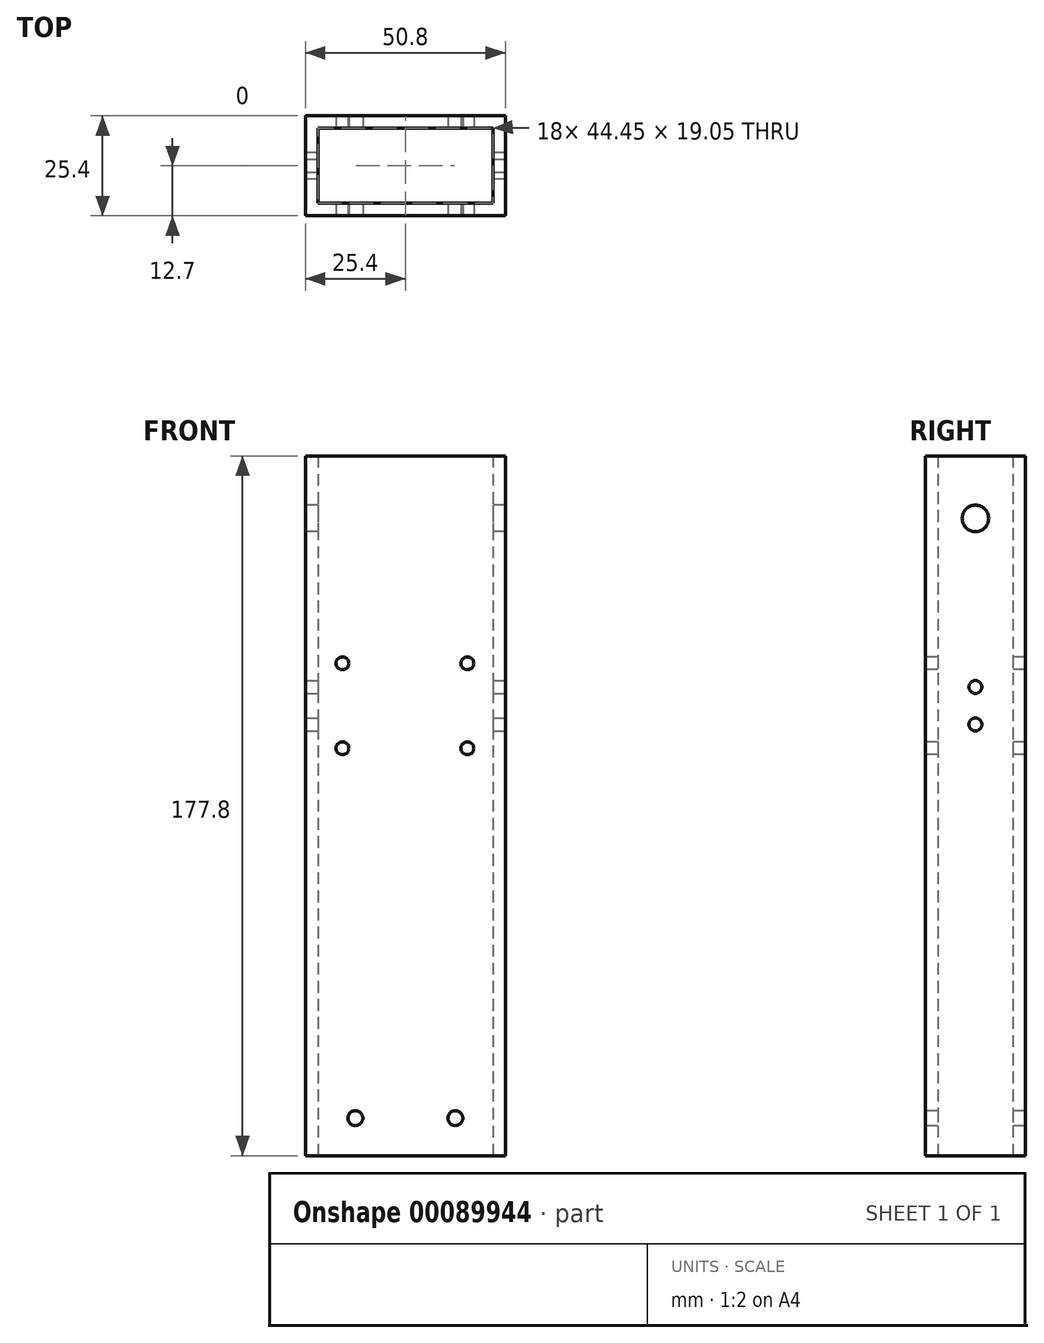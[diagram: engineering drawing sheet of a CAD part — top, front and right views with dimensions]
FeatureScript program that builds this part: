
annotation { "Feature Type Name" : "Feature", "Feature Type Description" : "" }
export const myFeature = defineFeature(function(context is Context, id is Id, definition is map)
    precondition{}
    {
        {
            var Q0;
            Q0=qCreatedBy(makeId("Top.planeOp"),FACE);
            var sketch = newSketch(context, id + "F0", { "sketchPlane" : qUnion([Q0])});
            skLineSegment(sketch, "E0.bottom", {"start": v(0, 0) * mm, "end": v(50.8, 0) * mm});
            skLineSegment(sketch, "E0.top", {"start": v(0, 25.4) * mm, "end": v(50.8, 25.4) * mm});
            skLineSegment(sketch, "E0.left", {"start": v(0, 0) * mm, "end": v(0, 25.4) * mm});
            skLineSegment(sketch, "E0.right", {"start": v(50.8, 0) * mm, "end": v(50.8, 25.4) * mm});
            skLineSegment(sketch, "E1.0", {"start": v(3.17, 22.23) * mm, "end": v(47.62, 22.23) * mm});
            skLineSegment(sketch, "E2.0", {"start": v(3.17, 3.18) * mm, "end": v(3.17, 22.23) * mm});
            skLineSegment(sketch, "E3.0", {"start": v(3.18, 3.18) * mm, "end": v(47.62, 3.18) * mm});
            skLineSegment(sketch, "E4.0", {"start": v(47.62, 3.18) * mm, "end": v(47.62, 22.23) * mm});
            skSolve(sketch);
        }
        {
            var Q0;
            Q0=makeQuery(id+"F0.imprint","IMPRINT",FACE,{"disambiguationData":[TD([[makeQuery(id+"F0.imprint","IMPRINT",EDGE,{"derivedFrom":sQuery(id+"F0.wireOp",EDGE,"E0.bottom")}),1.0]])]});
            extrude(context, id + "F1", {"entities" : qUnion([Q0]), "depth" : 177.8 * mm});
        }
        {
            var Q0;
            Q0=qCreatedBy(makeId("Right.planeOp"),FACE);
            var sketch = newSketch(context, id + "F2", { "sketchPlane" : qUnion([Q0])});
            skPoint(sketch, "E5", {"position": v(12.7, 161.93) * mm});
            skSolve(sketch);
        }
        {
            var Q0;
            Q0=sQuery(id+"F2.wireOp",VERTEX,"E5");
            var Q1;
            Q1=makeQuery(id+"F1.opExtrude","SWEPT_BODY",BODY,{"disambiguationData":[OSD([sQuery(id+"F0.wireOp",EDGE,"E0.bottom"),sQuery(id+"F0.wireOp",EDGE,"E0.top"),sQuery(id+"F0.wireOp",EDGE,"E0.left"),sQuery(id+"F0.wireOp",EDGE,"E0.right"),sQuery(id+"F0.wireOp",EDGE,"E1.0"),sQuery(id+"F0.wireOp",EDGE,"E2.0"),sQuery(id+"F0.wireOp",EDGE,"E3.0"),sQuery(id+"F0.wireOp",EDGE,"E4.0")])]});
            hole(context, id + "F3", {"style" : HoleStyle.SIMPLE, "endStyle" : HoleEndStyle.THROUGH, "oppositeDirection" : true, "standardTappedOrClearance" : lookupTablePath({ "standard" : "ANSI", "fit" : "Normal (ASME)", "size" : "1/4", "type" : "Clearance" }), "standardBlindInLast" : lookupTablePath({ "fit" : "Free", "standard" : "ANSI", "size" : "1/4", "type" : "Clearance" }), "holeDiameter" : 6.76 * mm, "locations" : qUnion([Q0]), "scope" : qUnion([Q1]), "isTappedThrough" : true});
        }
        {
            var Q0;
            Q0=makeQuery(id+"F1.opExtrude","SWEPT_FACE",FACE,{"disambiguationData":[OSD([sQuery(id+"F0.wireOp",EDGE,"E0.bottom")])]});
            var sketch = newSketch(context, id + "F4", { "sketchPlane" : qUnion([Q0])});
            skPoint(sketch, "E6", {"position": v(12.7, 9.53) * mm});
            skPoint(sketch, "E7", {"position": v(38.1, 9.53) * mm});
            skSolve(sketch);
        }
        {
            var Q0;
            Q0=sQuery(id+"F4.wireOp",VERTEX,"E6");
            var Q1;
            Q1=sQuery(id+"F4.wireOp",VERTEX,"E7");
            var Q2;
            Q2=makeQuery(id+"F1.opExtrude","SWEPT_BODY",BODY,{"disambiguationData":[OSD([sQuery(id+"F0.wireOp",EDGE,"E0.bottom"),sQuery(id+"F0.wireOp",EDGE,"E0.top"),sQuery(id+"F0.wireOp",EDGE,"E0.left"),sQuery(id+"F0.wireOp",EDGE,"E0.right"),sQuery(id+"F0.wireOp",EDGE,"E1.0"),sQuery(id+"F0.wireOp",EDGE,"E2.0"),sQuery(id+"F0.wireOp",EDGE,"E3.0"),sQuery(id+"F0.wireOp",EDGE,"E4.0")])]});
            hole(context, id + "F5", {"style" : HoleStyle.SIMPLE, "endStyle" : HoleEndStyle.THROUGH, "standardTappedOrClearance" : lookupTablePath({ "standard" : "ANSI", "fit" : "Normal (ASME)", "size" : "#6", "type" : "Clearance" }), "standardBlindInLast" : lookupTablePath({ "fit" : "Free", "standard" : "ANSI", "size" : "#6", "type" : "Clearance" }), "holeDiameter" : 3.8 * mm, "locations" : qUnion([Q0, Q1]), "scope" : qUnion([Q2]), "isTappedThrough" : true});
        }
        {
            var Q0;
            Q0=makeQuery(id+"F1.opExtrude","SWEPT_FACE",FACE,{"disambiguationData":[OSD([sQuery(id+"F0.wireOp",EDGE,"E0.bottom")])]});
            var sketch = newSketch(context, id + "F6", { "sketchPlane" : qUnion([Q0])});
            skPoint(sketch, "E8", {"position": v(9.4, 125.1) * mm});
            skPoint(sketch, "E9", {"position": v(41.15, 125.1) * mm});
            skPoint(sketch, "E10", {"position": v(9.4, 103.5) * mm});
            skPoint(sketch, "E11", {"position": v(41.15, 103.5) * mm});
            skSolve(sketch);
        }
        {
            var Q0;
            Q0=sQuery(id+"F6.wireOp",VERTEX,"E8");
            var Q1;
            Q1=sQuery(id+"F6.wireOp",VERTEX,"E9");
            var Q2;
            Q2=sQuery(id+"F6.wireOp",VERTEX,"E11");
            var Q3;
            Q3=sQuery(id+"F6.wireOp",VERTEX,"E10");
            var Q4;
            Q4=makeQuery(id+"F1.opExtrude","SWEPT_BODY",BODY,{"disambiguationData":[OSD([sQuery(id+"F0.wireOp",EDGE,"E0.bottom"),sQuery(id+"F0.wireOp",EDGE,"E0.top"),sQuery(id+"F0.wireOp",EDGE,"E0.left"),sQuery(id+"F0.wireOp",EDGE,"E0.right"),sQuery(id+"F0.wireOp",EDGE,"E1.0"),sQuery(id+"F0.wireOp",EDGE,"E2.0"),sQuery(id+"F0.wireOp",EDGE,"E3.0"),sQuery(id+"F0.wireOp",EDGE,"E4.0")])]});
            hole(context, id + "F7", {"style" : HoleStyle.SIMPLE, "endStyle" : HoleEndStyle.THROUGH, "standardTappedOrClearance" : lookupTablePath({ "standard" : "ANSI", "fit" : "Normal (ASME)", "size" : "#4", "type" : "Clearance" }), "standardBlindInLast" : lookupTablePath({ "fit" : "Free", "standard" : "ANSI", "size" : "#4", "type" : "Clearance" }), "holeDiameter" : 3.26 * mm, "locations" : qUnion([Q0, Q1, Q2, Q3]), "scope" : qUnion([Q4]), "isTappedThrough" : true});
        }
        {
            var Q0;
            Q0=makeQuery(id+"F1.opExtrude","SWEPT_FACE",FACE,{"disambiguationData":[OSD([sQuery(id+"F0.wireOp",EDGE,"E0.right")])]});
            var sketch = newSketch(context, id + "F8", { "sketchPlane" : qUnion([Q0])});
            skPoint(sketch, "E12", {"position": v(12.7, 119.06) * mm});
            skPoint(sketch, "E12.positionSnap0", {"position": v(12.7, 177.8) * mm});
            skPoint(sketch, "E13", {"position": v(12.7, 109.54) * mm});
            skPoint(sketch, "E14", {"position": v(12.7, 114.3) * mm});
            skSolve(sketch);
        }
        {
            var Q0;
            Q0=sQuery(id+"F8.wireOp",VERTEX,"E12");
            var Q1;
            Q1=sQuery(id+"F8.wireOp",VERTEX,"E13");
            var Q2;
            Q2=makeQuery(id+"F1.opExtrude","SWEPT_BODY",BODY,{"disambiguationData":[OSD([sQuery(id+"F0.wireOp",EDGE,"E0.bottom"),sQuery(id+"F0.wireOp",EDGE,"E0.top"),sQuery(id+"F0.wireOp",EDGE,"E0.left"),sQuery(id+"F0.wireOp",EDGE,"E0.right"),sQuery(id+"F0.wireOp",EDGE,"E1.0"),sQuery(id+"F0.wireOp",EDGE,"E2.0"),sQuery(id+"F0.wireOp",EDGE,"E3.0"),sQuery(id+"F0.wireOp",EDGE,"E4.0")])]});
            hole(context, id + "F9", {"style" : HoleStyle.SIMPLE, "endStyle" : HoleEndStyle.THROUGH, "standardTappedOrClearance" : lookupTablePath({ "standard" : "ANSI", "fit" : "Normal (ASME)", "size" : "#4", "type" : "Clearance" }), "standardBlindInLast" : lookupTablePath({ "fit" : "Free", "standard" : "ANSI", "size" : "#4", "type" : "Clearance" }), "holeDiameter" : 3.26 * mm, "locations" : qUnion([Q0, Q1]), "scope" : qUnion([Q2]), "isTappedThrough" : true});
        }
    });
